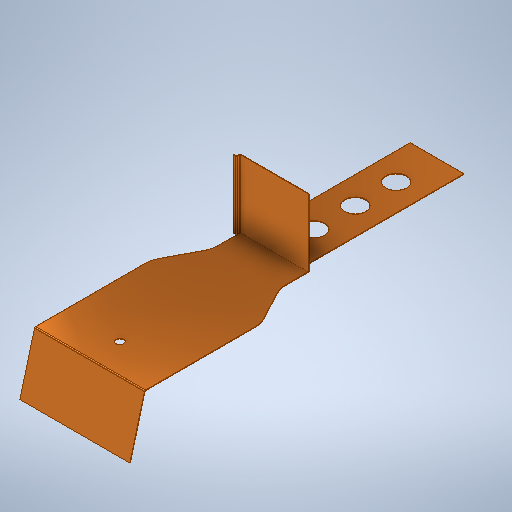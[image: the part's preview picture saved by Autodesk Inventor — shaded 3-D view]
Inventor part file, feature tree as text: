
AUTODESK INVENTOR PART (.ipt)
format: ipt  version: 2025.1 (Build 291241000, 241)  size: 397,312 bytes
history: native  units: mm
features: sheet_metal_op x13, sketch x10, other x5, extrude x3, hole x2, fillet x1
ambient origin geometry x8: Origin, YZ Plane, XZ Plane, XY Plane, X Axis, Y Axis, Z Axis, Center Point
bodies: Solid1 (feature_tree), Solid2 (feature_tree)
feature tree (34):
  sheet_metal_op  "Face1"
  sheet_metal_op  "Flange1"
  extrude  "Extrusion4"  Depth=94.0mm
  extrude  "Extrusion5"  Depth=0.5mm
  extrude  "Extrusion6"  Depth=1.0mm
  fillet  "Fillet1"  Radius=0.5mm
  sheet_metal_op  "Contour Flange1"
  hole  "Hole1"  [1 undecoded]
  hole  "Hole2"  [1 undecoded]
  sheet_metal_op  "Flange3"
  sheet_metal_op  "Flange4"
  sketch  "Sketch3"  dims[d2=94.0mm d3=133.0mm]
  other  "Plate1"
  sketch  "Sketch7"  dims[d4=0.5mm d16=0.5mm]
  other  "Plate2"
  sheet_metal_op  "Bend1"
  sheet_metal_op  "Corner1"
  sketch  "Sketch11"  dims[d17=0.25mm d18=1.0mm d19=0.5mm]
  sketch  "Sketch12"  dims[d20=49.0mm d21=75.0deg d22=0.5mm d23=2.0mm]
  sketch  "Sketch13"  dims[d24=0.5mm d25=0.5mm]
  sketch  "Sketch15"  dims[d45=34.0mm]
  other  "Plate4"
  sheet_metal_op  "Bend3"
  sheet_metal_op  "Corner3"
  sketch  "Sketch16"  dims[d46=29.0mm]
  sketch  "Sketch17"  dims[d48=34.0mm]
  sketch  "Sketch18"  dims[d49=29.0mm]
  other  "Plate5"
  sheet_metal_op  "Bend4"
  sheet_metal_op  "Corner4"
  sketch  "Sketch19"  dims[d50=10.0mm d51=0.0mm d52=58.0mm d53=0.5mm d54=25.0mm d55=0.0mm d56=0.5mm d57=46.0mm d58=138.5mm d59=0.0mm d60=6.0mm d62=20.0mm d63=0.5mm d64=0.5mm d65=0.25mm d66=1.0mm d67=0.5mm d68=58.0mm d69=0.5mm d70=0.5mm d71=2.0mm d72=0.5mm d73=0.5mm d74=6.647mm d75=16.0mm d76=4.0mm d77=2.0mm d78=90.0deg d79=0.5mm d80=0.0mm d81=25.0mm d82=35.0mm d83=35.0mm d84=35.0mm d85=23.0mm d86=18.0mm d87=6.0mm d88=4.0mm d89=2.0mm d90=90.0deg d91=8.0mm d92=0.0mm d93=0.5mm d94=0.25mm d95=1.0mm d96=0.5mm d97=3.0mm d98=90.0deg d99=0.5mm d100=2.0mm d101=0.5mm d102=0.5mm d103=0.5mm d104=0.25mm d105=1.0mm d106=0.5mm d107=3.0mm d108=90.0deg d109=0.5mm d110=2.0mm d111=0.5mm d112=0.5mm]
  other  "Plate6"
  sheet_metal_op  "Bend5"
  sheet_metal_op  "Corner5"
note: 2 required parameter values undecoded (feature->parameter linkage not recoverable at this tier; creation-order binding heuristic only, values carry confidence <= 0.55)
